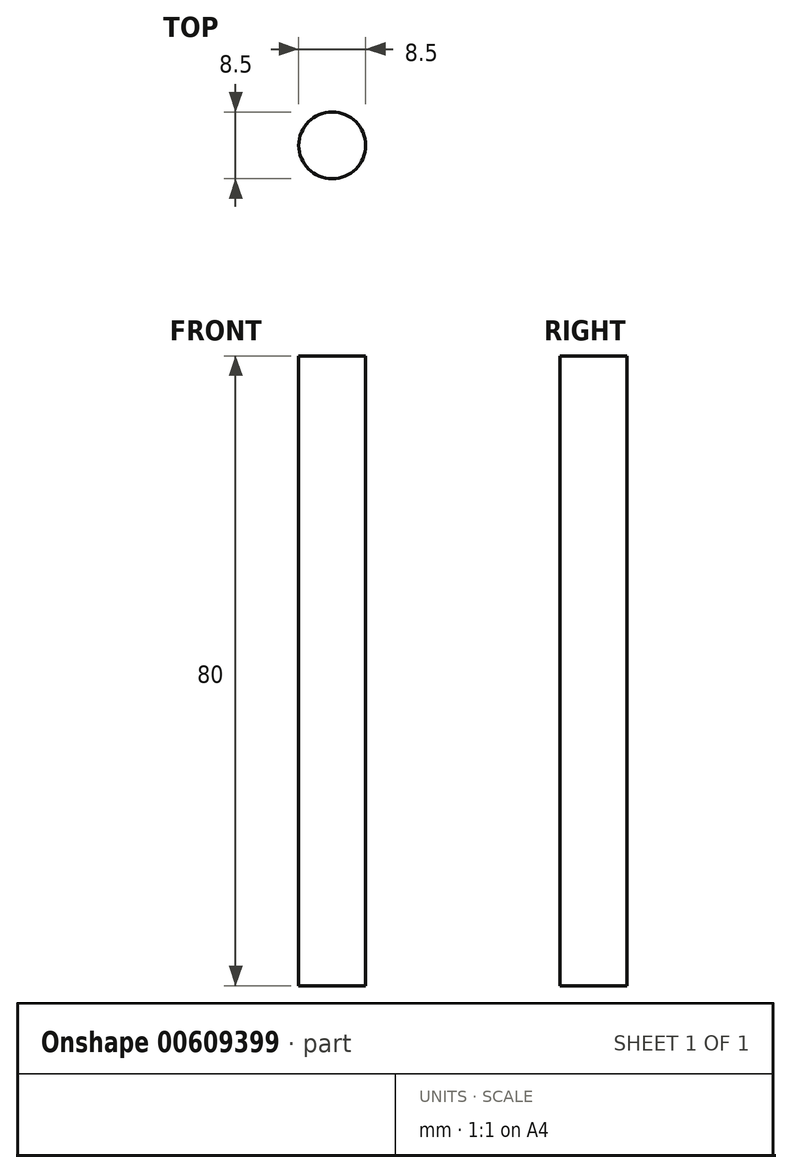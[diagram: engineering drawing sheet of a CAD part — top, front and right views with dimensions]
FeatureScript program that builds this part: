
annotation { "Feature Type Name" : "Feature", "Feature Type Description" : "" }
export const myFeature = defineFeature(function(context is Context, id is Id, definition is map)
    precondition{}
    {
        {
            var Q0;
            Q0=qCreatedBy(makeId("Top.planeOp"),FACE);
            var sketch = newSketch(context, id + "F0", { "sketchPlane" : qUnion([Q0])});
            skCircle(sketch, "E0", {"center": v(0, 0) * mm, "radius": 4.25 * mm});
            skSolve(sketch);
        }
        {
            var Q0;
            Q0=makeQuery(id+"F0.imprint","IMPRINT",FACE,{"disambiguationData":[TD([[makeQuery(id+"F0.imprint","IMPRINT",EDGE,{"derivedFrom":sQuery(id+"F0.wireOp",EDGE,"E0")}),1.0]])]});
            extrude(context, id + "F1", {"entities" : qUnion([Q0]), "depth" : 80 * mm, "offsetDistance" : 25 * mm});
        }
    });
